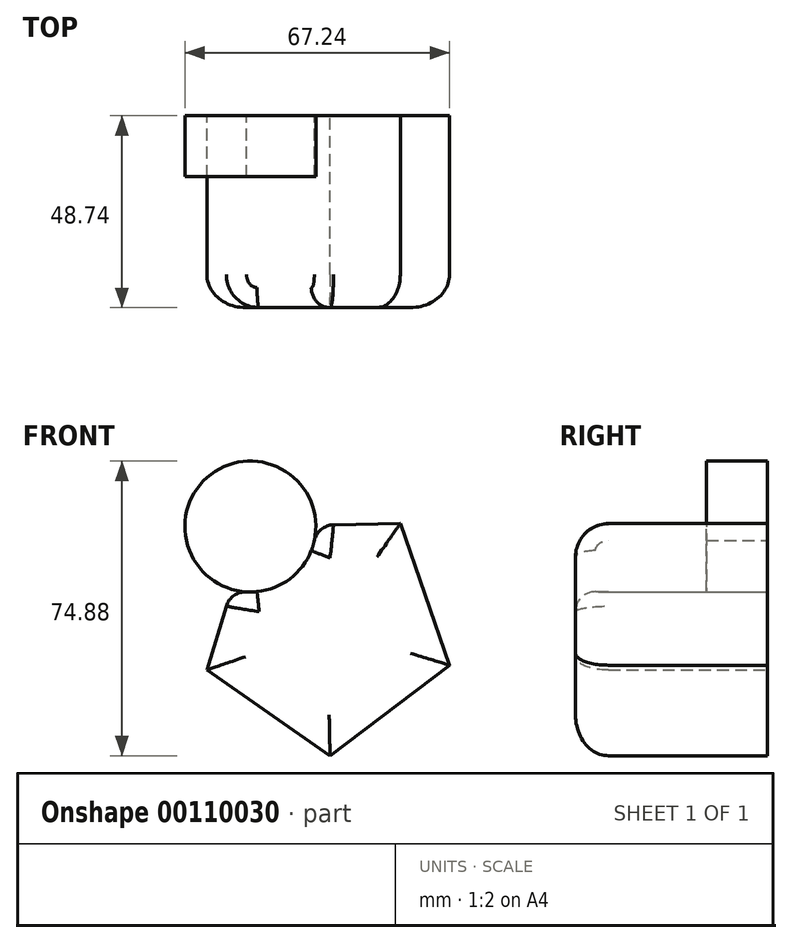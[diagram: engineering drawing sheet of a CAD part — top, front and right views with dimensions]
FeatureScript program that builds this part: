
annotation { "Feature Type Name" : "Feature", "Feature Type Description" : "" }
export const myFeature = defineFeature(function(context is Context, id is Id, definition is map)
    precondition{}
    {
        {
            var Q0;
            Q0=qCreatedBy(makeId("Front.planeOp"),FACE);
            var sketch = newSketch(context, id + "F0", { "sketchPlane" : qUnion([Q0])});
            skCircle(sketch, "E0.cCircle", {"center": v(-37.5, 29.07) * mm, "radius": 26.23 * mm, "construction": true});
            skLineSegment(sketch, "E0.0", {"start": v(-6.47, 19.68) * mm, "end": v(-36.84, -3.34) * mm});
            skLineSegment(sketch, "E0.1", {"start": v(-36.84, -3.34) * mm, "end": v(-68.11, 18.43) * mm});
            skLineSegment(sketch, "E0.2", {"start": v(-68.11, 18.43) * mm, "end": v(-61.9, 38.98) * mm});
            skLineSegment(sketch, "E0.3", {"start": v(-40.44, 55.24) * mm, "end": v(-18.97, 55.67) * mm});
            skLineSegment(sketch, "E0.4", {"start": v(-18.97, 55.67) * mm, "end": v(-6.47, 19.68) * mm});
            skPoint(sketch, "E0.0.midPoint", {"position": v(-21.65, 8.17) * mm});
            skCircle(sketch, "E1", {"center": v(-57.07, 54.9) * mm, "radius": 16.63 * mm});
            skSolve(sketch);
        }
        {
            var Q0;
            Q0=makeQuery(id+"F0.imprint","IMPRINT",FACE,{"disambiguationData":[TD([[makeQuery(id+"F0.imprint","IMPRINT",EDGE,{"derivedFrom":sQuery(id+"F0.wireOp",EDGE,"E0.0")}),-1.0]])]});
            extrude(context, id + "F1", {"entities" : qUnion([Q0]), "depth" : 48.74 * mm});
        }
        {
            var Q0;
            Q0=makeQuery(id+"F1.opExtrude","CAP_EDGE",EDGE,{"disambiguationData":[OSD([sQuery(id+"F0.wireOp",EDGE,"E0.3")])],"isStart":false});
            var Q1;
            Q1=makeQuery(id+"F1.opExtrude","CAP_EDGE",EDGE,{"disambiguationData":[OSD([sQuery(id+"F0.wireOp",EDGE,"E0.4")])],"isStart":false});
            var Q2;
            Q2=makeQuery(id+"F1.opExtrude","CAP_EDGE",EDGE,{"disambiguationData":[OSD([sQuery(id+"F0.wireOp",EDGE,"E0.0")])],"isStart":false});
            var Q3;
            Q3=makeQuery(id+"F1.opExtrude","CAP_EDGE",EDGE,{"disambiguationData":[OSD([sQuery(id+"F0.wireOp",EDGE,"E0.1")])],"isStart":false});
            var Q4;
            Q4=makeQuery(id+"F1.opExtrude","CAP_EDGE",EDGE,{"disambiguationData":[OSD([sQuery(id+"F0.wireOp",EDGE,"E0.2")])],"isStart":false});
            fillet(context, id + "F2", {"entities" : qUnion([Q0, Q1, Q2, Q3, Q4]), "radius" : 8.4 * mm, "tangentPropagation" : true, "allowEdgeOverflow" : false});
        }
        {
            var Q0;
            Q0=makeQuery(id+"F1.opExtrude","SWEPT_EDGE",EDGE,{"disambiguationData":[OSD([sQuery(id+"F0.wireOp",EDGE,"E0.2"),sQuery(id+"F0.wireOp",EDGE,"E1")])]});
            var Q1;
            Q1=makeQuery(id+"F2.opFillet","BLEND_EDGE",EDGE,{"blendedFrom":[makeQuery(id+"F1.opExtrude","CAP_EDGE",EDGE,{"disambiguationData":[OSD([sQuery(id+"F0.wireOp",EDGE,"E0.2")])],"isStart":false}),makeQuery(id+"F1.opExtrude","SWEPT_FACE",FACE,{"disambiguationData":[OSD([sQuery(id+"F0.wireOp",EDGE,"E1")])]})],"blendedInto":[makeQuery(id+"F1.opExtrude","SWEPT_FACE",FACE,{"disambiguationData":[OSD([sQuery(id+"F0.wireOp",EDGE,"E1")])]})]});
            fillet(context, id + "F3", {"entities" : qUnion([Q0, Q1]), "radius" : 5.08 * mm, "tangentPropagation" : true, "allowEdgeOverflow" : false});
        }
        {
            var Q0;
            {var subQ0=sQuery(id+"F0.wireOp",EDGE,"E1");var subQ1=makeQuery(id+"F0.imprint","INTERSECT",VERTEX,{"derivedFrom":[sQuery(id+"F0.wireOp",EDGE,"E0.2"),subQ0]});Q0=makeQuery(id+"F0.imprint","IMPRINT",FACE,{"disambiguationData":[TD([[makeQuery(id+"F0.imprint","IMPRINT",EDGE,{"disambiguationData":[TD([[subQ1,1.0]])],"derivedFrom":subQ0}),1.0]])]});}
            extrude(context, id + "F4", {"entities" : qUnion([Q0]), "operationType" : NewBodyOperationType.ADD, "depth" : 15.5 * mm});
        }
    });
